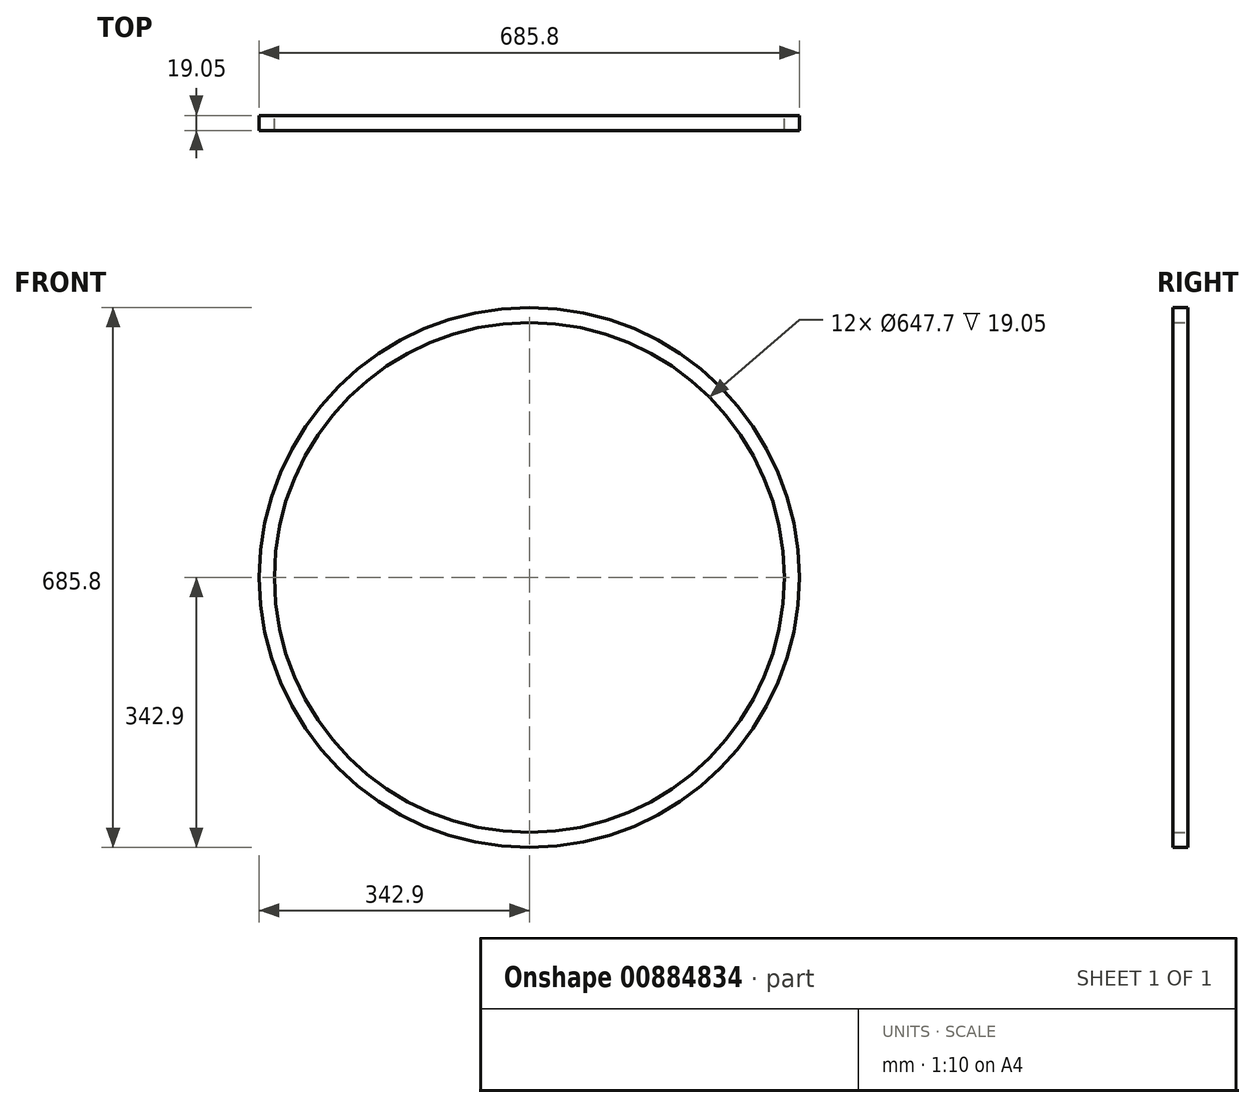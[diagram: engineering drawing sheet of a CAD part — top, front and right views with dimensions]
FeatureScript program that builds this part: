
annotation { "Feature Type Name" : "Feature", "Feature Type Description" : "" }
export const myFeature = defineFeature(function(context is Context, id is Id, definition is map)
    precondition{}
    {
        {
            var Q0;
            Q0=qCreatedBy(makeId("Front.planeOp"),FACE);
            var sketch = newSketch(context, id + "F0", { "sketchPlane" : qUnion([Q0])});
            skCircle(sketch, "E0", {"center": v(0, 0) * mm, "radius": 323.85 * mm});
            skCircle(sketch, "E1", {"center": v(0, 0) * mm, "radius": 342.9 * mm});
            skSolve(sketch);
        }
        {
            var Q0;
            Q0=makeQuery(id+"F0.imprint","IMPRINT",FACE,{"disambiguationData":[TD([[makeQuery(id+"F0.imprint","IMPRINT",EDGE,{"derivedFrom":sQuery(id+"F0.wireOp",EDGE,"E0")}),-1.0]])]});
            extrude(context, id + "F1", {"entities" : qUnion([Q0]), "depth" : 19.05 * mm, "offsetDistance" : 25.4 * mm});
        }
    });
